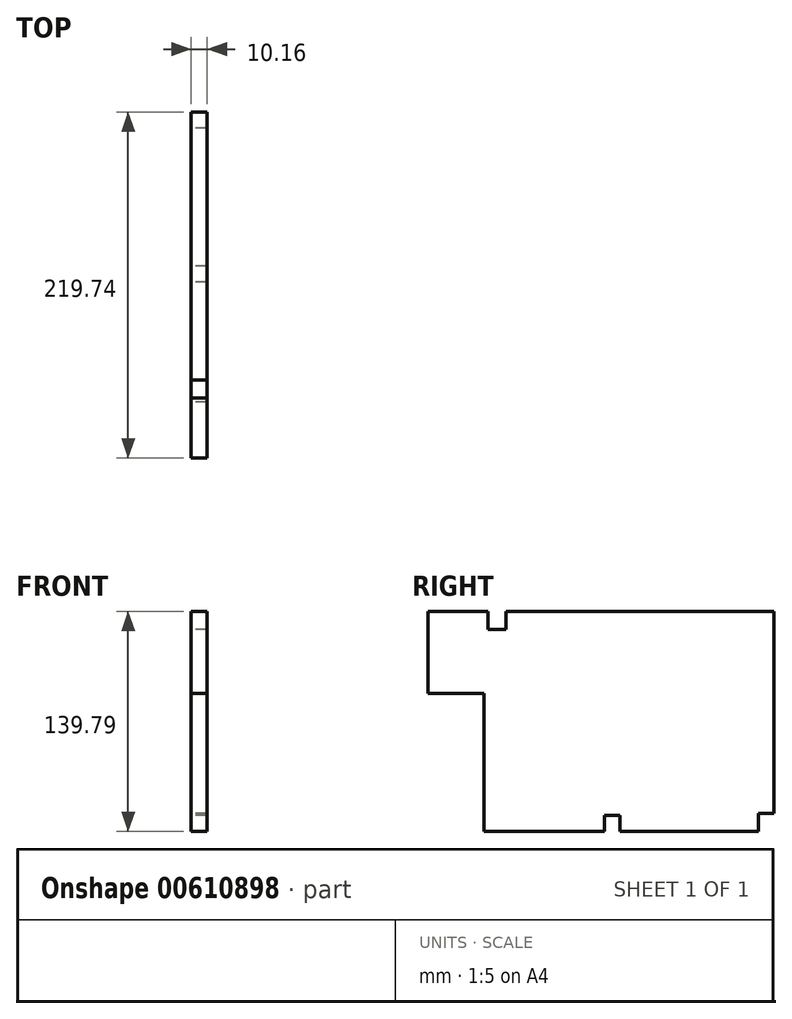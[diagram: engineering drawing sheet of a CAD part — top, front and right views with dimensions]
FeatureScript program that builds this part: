
annotation { "Feature Type Name" : "Feature", "Feature Type Description" : "" }
export const myFeature = defineFeature(function(context is Context, id is Id, definition is map)
    precondition{}
    {
        {
            var Q0;
            Q0=qCreatedBy(makeId("Right.planeOp"),FACE);
            var sketch = newSketch(context, id + "F0", { "sketchPlane" : qUnion([Q0])});
            skLineSegment(sketch, "E0", {"start": v(-43.27, -29.45) * mm, "end": v(-203.32, -29.45) * mm});
            skLineSegment(sketch, "E1", {"start": v(-203.32, -29.45) * mm, "end": v(-203.32, -40.87) * mm});
            skLineSegment(sketch, "E2", {"start": v(-203.32, -40.87) * mm, "end": v(-214.77, -40.87) * mm});
            skLineSegment(sketch, "E3", {"start": v(-214.77, -40.87) * mm, "end": v(-214.77, -29.45) * mm});
            skLineSegment(sketch, "E4", {"start": v(-214.77, -29.45) * mm, "end": v(-252.89, -29.45) * mm});
            skLineSegment(sketch, "E5", {"start": v(-252.89, -29.45) * mm, "end": v(-252.89, -81.55) * mm});
            skLineSegment(sketch, "E6", {"start": v(-252.89, -81.55) * mm, "end": v(-217.32, -81.55) * mm});
            skLineSegment(sketch, "E7", {"start": v(-217.32, -81.55) * mm, "end": v(-217.32, -169.24) * mm});
            skLineSegment(sketch, "E8", {"start": v(-217.32, -169.24) * mm, "end": v(-141.09, -169.24) * mm});
            skLineSegment(sketch, "E9", {"start": v(-141.09, -169.24) * mm, "end": v(-141.09, -159.1) * mm});
            skLineSegment(sketch, "E10", {"start": v(-141.09, -159.1) * mm, "end": v(-130.94, -159.1) * mm});
            skLineSegment(sketch, "E11", {"start": v(-130.94, -159.1) * mm, "end": v(-130.94, -169.24) * mm});
            skLineSegment(sketch, "E12", {"start": v(-130.94, -169.24) * mm, "end": v(-43.27, -169.24) * mm});
            skLineSegment(sketch, "E13", {"start": v(-43.27, -29.45) * mm, "end": v(-33.15, -29.45) * mm});
            skLineSegment(sketch, "E14", {"start": v(-33.15, -29.45) * mm, "end": v(-33.15, -157.77) * mm});
            skLineSegment(sketch, "E15", {"start": v(-33.15, -157.77) * mm, "end": v(-43.27, -157.77) * mm});
            skLineSegment(sketch, "E16", {"start": v(-43.27, -157.77) * mm, "end": v(-43.27, -169.24) * mm});
            skSolve(sketch);
        }
        {
            var Q0;
            Q0=makeQuery(id+"F0.imprint","IMPRINT",FACE,{"disambiguationData":[TD([[makeQuery(id+"F0.imprint","IMPRINT",EDGE,{"derivedFrom":sQuery(id+"F0.wireOp",EDGE,"E0")}),1.0]])]});
            extrude(context, id + "F1", {"entities" : qUnion([Q0]), "depth" : 10.16 * mm, "offsetDistance" : 25.4 * mm});
        }
    });
